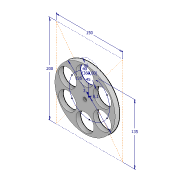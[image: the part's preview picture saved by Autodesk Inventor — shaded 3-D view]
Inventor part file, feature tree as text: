
AUTODESK INVENTOR PART (.ipt)
format: ipt  version: 2021 (Build 250183000, 183)  size: 119,296 bytes
history: native  units: mm
features: extrude x2, sketch x1
ambient origin geometry x8: Origin, YZ Plane, XZ Plane, XY Plane, X Axis, Y Axis, Z Axis, Center Point
bodies: Solid1 (feature_tree)
feature tree (3):
  sketch  "Sketch1"  dims[d0=56.0mm d1=150.0mm d2=200.0mm d3=135.0mm d4=40.0mm d5=60.0mm d7=360.0deg d9=45.0mm d10=135.0mm d11=3.0mm d12=8.1mm d13=10.0mm d14=0.0mm d15=7.0mm d16=0.0mm]
  extrude  "Extrusion1"  Depth=7.0mm
  extrude  "Extrusion2"  Depth=7.0mm
